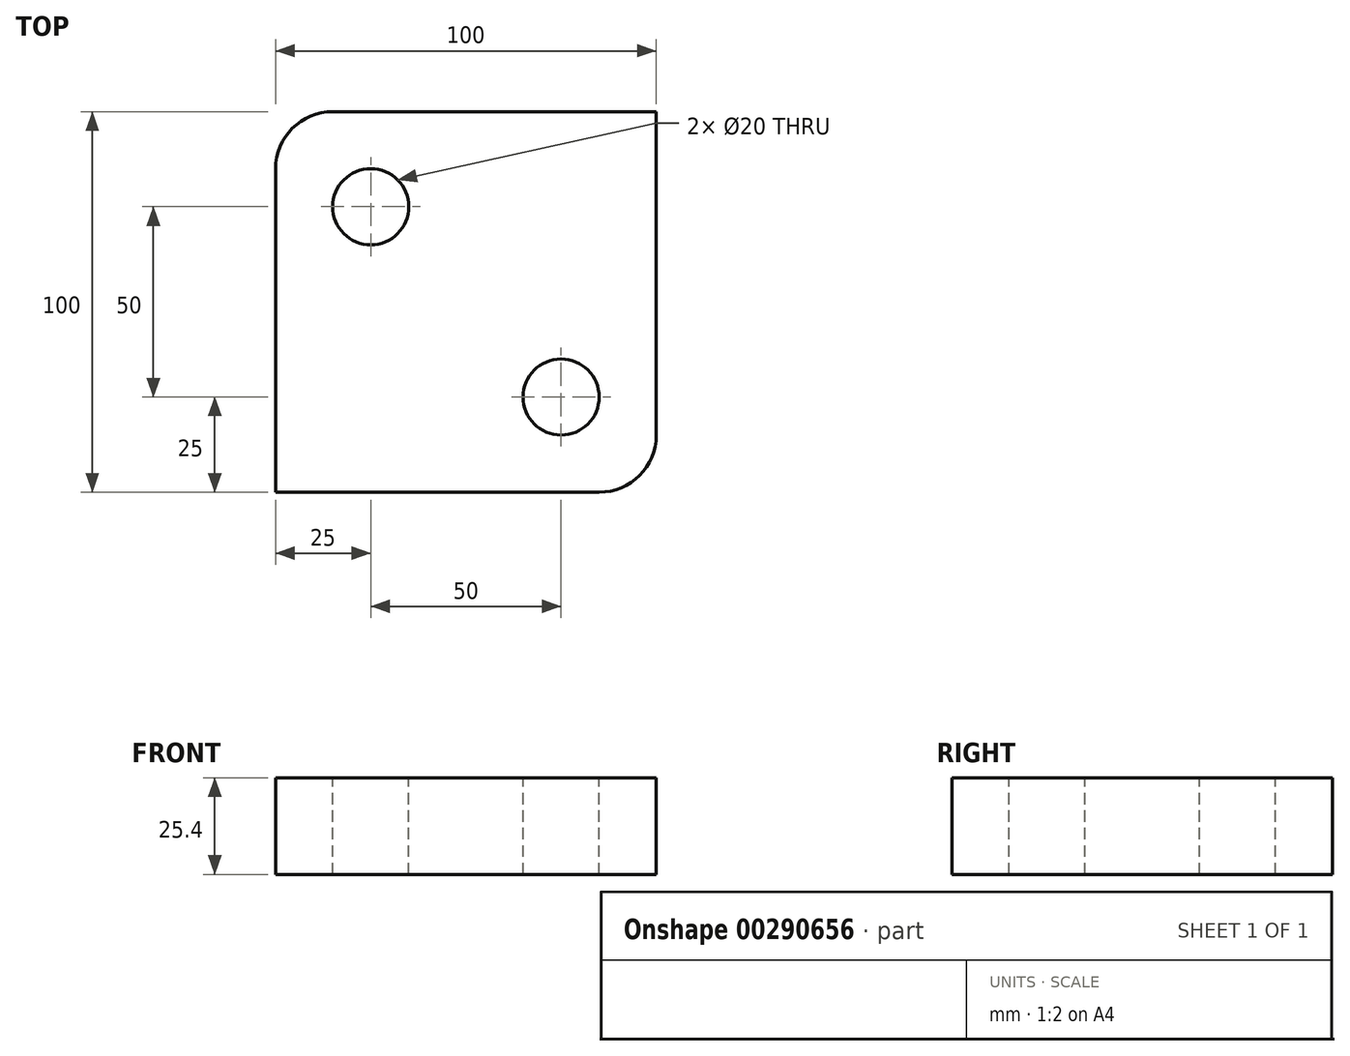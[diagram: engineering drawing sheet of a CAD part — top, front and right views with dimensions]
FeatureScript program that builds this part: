
annotation { "Feature Type Name" : "Feature", "Feature Type Description" : "" }
export const myFeature = defineFeature(function(context is Context, id is Id, definition is map)
    precondition{}
    {
        {
            var Q0;
            Q0=qCreatedBy(makeId("Top.planeOp"),FACE);
            var sketch = newSketch(context, id + "F0", { "sketchPlane" : qUnion([Q0])});
            skLineSegment(sketch, "E0.bottom", {"start": v(-35, 50) * mm, "end": v(50, 50) * mm});
            skLineSegment(sketch, "E0.top", {"start": v(-50, -50) * mm, "end": v(35, -50) * mm});
            skLineSegment(sketch, "E0.left", {"start": v(-50, 35) * mm, "end": v(-50, -50) * mm});
            skLineSegment(sketch, "E0.right", {"start": v(50, 50) * mm, "end": v(50, -35) * mm});
            skPoint(sketch, "E0.middle", {"position": v(0, 0) * mm});
            skPoint(sketch, "E1.visualSharp", {"position": v(-50, 50) * mm});
            skArc(sketch, "E1.filletArc", {"start": v(-35, 50) * mm, "mid": v(-45.6, 45.6) * mm, "end": v(-50, 35) * mm});
            skPoint(sketch, "E2.visualSharp", {"position": v(50, -50) * mm});
            skArc(sketch, "E2.filletArc", {"start": v(35, -50) * mm, "mid": v(45.6, -45.6) * mm, "end": v(50, -35) * mm});
            skSolve(sketch);
        }
        {
            var Q0;
            Q0=makeQuery(id+"F0.imprint","IMPRINT",FACE,{"disambiguationData":[TD([[makeQuery(id+"F0.imprint","IMPRINT",EDGE,{"derivedFrom":sQuery(id+"F0.wireOp",EDGE,"E0.bottom")}),-1.0]])]});
            extrude(context, id + "F1", {"entities" : qUnion([Q0]), "depth" : 25.4 * mm});
        }
        {
            var Q0;
            Q0=makeQuery(id+"F1.opExtrude","CAP_FACE",FACE,{"disambiguationData":[OSD([sQuery(id+"F0.wireOp",EDGE,"E0.bottom"),sQuery(id+"F0.wireOp",EDGE,"E0.top"),sQuery(id+"F0.wireOp",EDGE,"E0.left"),sQuery(id+"F0.wireOp",EDGE,"E0.right"),sQuery(id+"F0.wireOp",EDGE,"E1.filletArc"),sQuery(id+"F0.wireOp",EDGE,"E2.filletArc")])],"isStart":false});
            var sketch = newSketch(context, id + "F2", { "sketchPlane" : qUnion([Q0])});
            skCircle(sketch, "E3", {"center": v(-25, 25) * mm, "radius": 10 * mm});
            skCircle(sketch, "E4", {"center": v(25, -25) * mm, "radius": 10 * mm});
            skSolve(sketch);
        }
        {
            var Q0;
            Q0=makeQuery(id+"F2.imprint","IMPRINT",FACE,{"disambiguationData":[TD([[makeQuery(id+"F2.imprint","IMPRINT",EDGE,{"derivedFrom":sQuery(id+"F2.wireOp",EDGE,"E3")}),1.0]])]});
            var Q1;
            Q1=makeQuery(id+"F2.imprint","IMPRINT",FACE,{"disambiguationData":[TD([[makeQuery(id+"F2.imprint","IMPRINT",EDGE,{"derivedFrom":sQuery(id+"F2.wireOp",EDGE,"E4")}),1.0]])]});
            extrude(context, id + "F3", {"entities" : qUnion([Q0, Q1]), "operationType" : NewBodyOperationType.REMOVE, "endBound" : BoundingType.UP_TO_NEXT, "oppositeDirection" : true, "depth" : 25 * mm});
        }
    });
